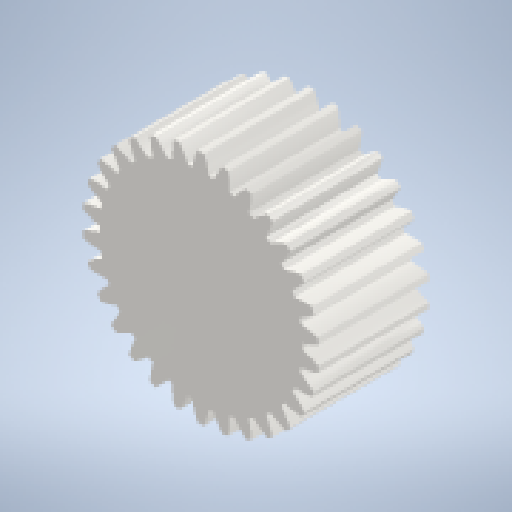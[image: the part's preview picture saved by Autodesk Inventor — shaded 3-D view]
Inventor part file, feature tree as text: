
AUTODESK INVENTOR PART (.ipt)
format: ipt  version: 2024 (Build 280153000, 153)  size: 283,648 bytes
history: native  units: mm (DEFAULTED — no unit token found)
features: plane x3, other x3, extrude x1, sketch x1
ambient origin geometry x8: Origin, YZ Plane, XZ Plane, XY Plane, X Axis, Y Axis, Z Axis, Center Point
bodies: Solid1 (feature_tree)
feature tree (8):
  extrude  "Extrusion1"  Depth=30.0mm TaperAngle=0.0deg
  plane  "Work Plane2"
  plane  "Work Plane8"
  plane  "Work Plane9"
  other  "Spur Gear"
  sketch  "Sketch1"  dims[d0=64.0mm d1=30.0mm d2=0.0mm d3=60.0mm d4=10.0mm d5=0.0mm d16=40.0mm d17=0.0mm d34=1.047198mm d39=0.0mm d41=0.0mm d43=40.0mm d46=40.0mm d47=0.0mm d48=0.0mm]
  other  "Srf1"
  other  "Pitch Diameter"
